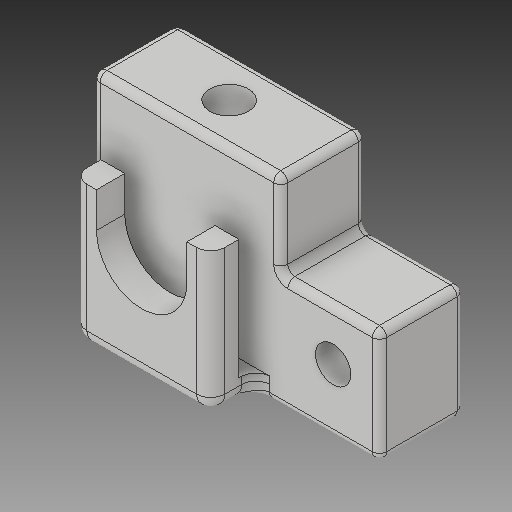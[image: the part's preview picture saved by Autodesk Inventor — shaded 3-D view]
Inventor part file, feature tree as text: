
AUTODESK INVENTOR PART (.ipt)
format: ipt  version: 2018 (Build 220112000, 112)  size: 379,392 bytes
history: native  units: in
note: dims shown in document units (in); Inventor stores cm internally (conversion verified against a paired STEP export)
features: sketch x24, plane x4, other x3
ambient origin geometry x8: Origin, YZ Plane, XZ Plane, XY Plane, X Axis, Y Axis, Z Axis, Center Point
bodies: Solid1 (feature_tree)
feature tree (31):
  other  "SyringeTailLeverAttachment.ipt"
  other  "Solid2::SyringeTailLeverAttachment.ipt"
  other  "TaggingFeature1"
  sketch  "Sketch2"  dims[d0=0.3937in]
  sketch  "Sketch3"
  sketch  "Sketch5"
  sketch  "Sketch6"
  sketch  "Sketch7"
  sketch  "Sketch8"
  sketch  "Sketch9"
  sketch  "Sketch10"
  sketch  "Sketch11"
  sketch  "Sketch12"
  sketch  "Sketch13"
  sketch  "Sketch14"
  sketch  "Sketch15"
  sketch  "Sketch16"
  sketch  "Sketch17"
  sketch  "Sketch18"
  sketch  "Sketch19"
  sketch  "Sketch21"
  sketch  "Sketch22"
  sketch  "Sketch23"
  sketch  "Sketch24"
  sketch  "Sketch27"
  sketch  "Sketch28"
  sketch  "Sketch29"
  plane  "Work Plane1"
  plane  "Work Plane2"
  plane  "Work Plane3"
  plane  "Work Plane4"
